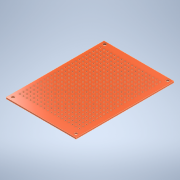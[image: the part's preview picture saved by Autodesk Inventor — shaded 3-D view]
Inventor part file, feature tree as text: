
AUTODESK INVENTOR PART (.ipt)
format: ipt  version: 2022 (Build 260153000, 153)  size: 702,464 bytes
history: native  units: mm
features: extrude x2, sketch x2
ambient origin geometry x8: Origin, YZ Plane, XZ Plane, XY Plane, X Axis, Y Axis, Z Axis, Center Point
bodies: Solid1 (feature_tree)
feature tree (4):
  extrude  "Extrusion1"  Depth=50.0mm
  extrude  "Extrusion2"  Depth=1.0mm
  sketch  "Sketch1"  dims[d0=70.0mm d1=50.0mm]
  sketch  "Sketch2"  dims[d2=1.0mm d3=0.0mm d4=2.0mm d5=2.5mm d6=2.0mm d7=0.0mm d8=0.0mm d9=2.5mm d10=2.5mm d11=2.0mm d12=3.0mm d13=5.5mm d14=1.0mm d15=240.0mm d17=2.5mm d18=180.0mm d20=2.5mm]
